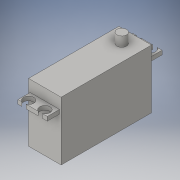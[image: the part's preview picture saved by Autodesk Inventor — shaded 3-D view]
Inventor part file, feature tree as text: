
AUTODESK INVENTOR PART (.ipt)
format: ipt  version: 2016 (Build 200138000, 138)  size: 145,920 bytes
history: native  units: in
note: dims shown in document units (in); Inventor stores cm internally (conversion verified against a paired STEP export)
features: sketch x7, extrude x4, hole x2
ambient origin geometry x8: Origin, YZ Plane, XZ Plane, XY Plane, X Axis, Y Axis, Z Axis, Center Point
bodies: Body1 (feature_tree)
feature tree (13):
  sketch  "Sketch5"  dims[d18=0.7874in d19=2.185in]
  extrude  "Extrusion4"  Depth=2.185in
  extrude  "Extrusion5"  Depth=0.0984in
  extrude  "Extrusion6"  Depth=0.2953in TaperAngle=0.0deg
  extrude  "Extrusion7"  Depth=0.2362in TaperAngle=0.0deg
  hole  "Hole1"  [1 undecoded]
  hole  "Hole2"  [1 undecoded]
  sketch  "Sketch6"  dims[d20=1.4213in d21=0.0in d25=0.0984in]
  sketch  "Sketch7"  dims[d26=0.2953in d27=0.0in d32=0.2953in d33=0.0in]
  sketch  "Sketch8"  dims[d35=0.2323in d36=0.2362in d37=0.0in]
  sketch  "Sketch9"  dims[d39=0.3937in d40=0.3248in]
  sketch  "Sketch11"  dims[d48=0.1772in d50=0.1772in]
  sketch  "Sketch15"  dims[d51=0.25in d52=0.75in d53=0.375in d54=0.25in d55=0.5635in d56=1.0in d57=0.8108in d64=0.1772in d66=0.1772in d67=0.25in d68=0.75in d69=0.375in d70=0.25in d71=0.5635in d72=1.0in d73=0.8108in]
note: 2 required parameter values undecoded (feature->parameter linkage not recoverable at this tier; creation-order binding heuristic only, values carry confidence <= 0.55)
